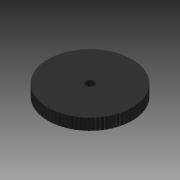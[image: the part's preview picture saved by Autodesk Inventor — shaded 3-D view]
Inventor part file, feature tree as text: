
AUTODESK INVENTOR PART (.ipt)
format: ipt  version: 2014 (Build 180170000, 170)  size: 393,728 bytes
history: native  units: in
note: dims shown in document units (in); Inventor stores cm internally (conversion verified against a paired STEP export)
features: other x3, sketch x3
ambient origin geometry x8: Origin, YZ Plane, XZ Plane, XY Plane, X Axis, Y Axis, Z Axis, Center Point
bodies: Solid1 (feature_tree)
feature tree (6):
  other  "wheel 1.ipt"
  other  "Solid1::wheel 1.ipt"
  other  "TaggingFeature1"
  sketch  "Sketch1"  dims[d0=0.3937in]
  sketch  "Sketch2"  dims[d1=0.3937in d2=0.0in d3=0.2756in d4=0.3937in d5=0.0in d7=0.3937in d8=0.0in d9=31.4961in d10=360.0deg]
  sketch  "Sketch3"
